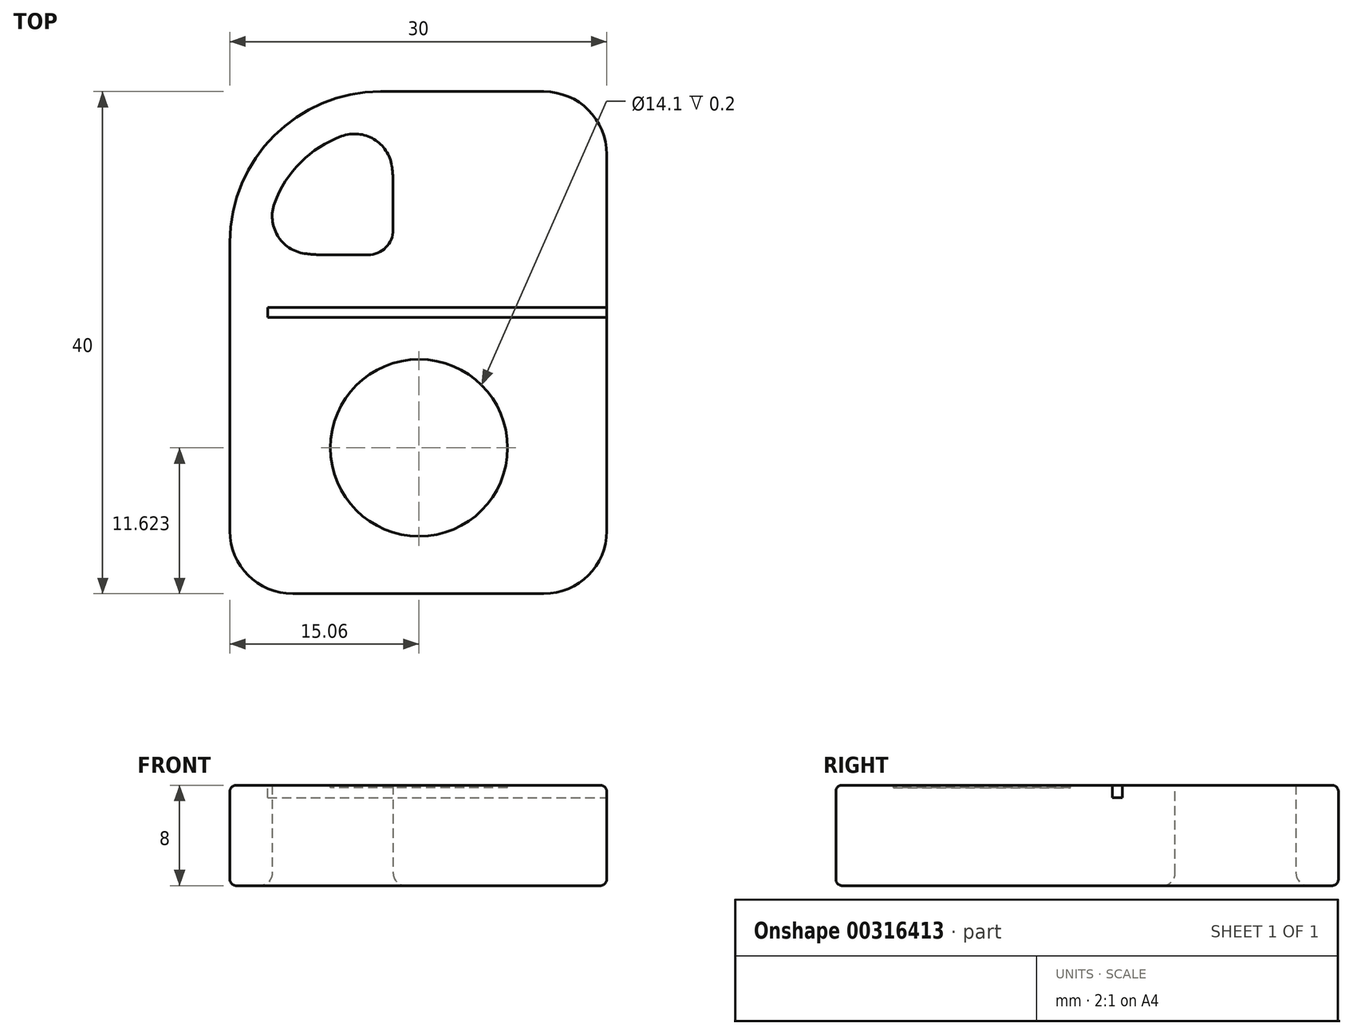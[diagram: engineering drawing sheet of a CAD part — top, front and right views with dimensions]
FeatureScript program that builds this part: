
annotation { "Feature Type Name" : "Feature", "Feature Type Description" : "" }
export const myFeature = defineFeature(function(context is Context, id is Id, definition is map)
    precondition{}
    {
        {
            var Q0;
            Q0=qCreatedBy(makeId("Top.planeOp"),FACE);
            var sketch = newSketch(context, id + "F0", { "sketchPlane" : qUnion([Q0])});
            skLineSegment(sketch, "E0.bottom", {"start": v(0, 0) * mm, "end": v(30, 0) * mm});
            skLineSegment(sketch, "E0.top", {"start": v(0, -40) * mm, "end": v(30, -40) * mm});
            skLineSegment(sketch, "E0.left", {"start": v(0, 0) * mm, "end": v(0, -40) * mm});
            skLineSegment(sketch, "E0.right", {"start": v(30, 0) * mm, "end": v(30, -40) * mm});
            skSolve(sketch);
        }
        {
            var Q0;
            Q0=makeQuery(id+"F0.imprint","IMPRINT",FACE,{"disambiguationData":[TD([[makeQuery(id+"F0.imprint","IMPRINT",EDGE,{"derivedFrom":sQuery(id+"F0.wireOp",EDGE,"E0.bottom")}),-1.0]])]});
            extrude(context, id + "F1", {"entities" : qUnion([Q0]), "depth" : 8 * mm});
        }
        {
            var Q0;
            Q0=makeQuery(id+"F1.opExtrude","SWEPT_EDGE",EDGE,{"disambiguationData":[OSD([sQuery(id+"F0.wireOp",EDGE,"E0.bottom"),sQuery(id+"F0.wireOp",EDGE,"E0.left")])]});
            fillet(context, id + "F2", {"entities" : qUnion([Q0]), "radius" : 12 * mm, "tangentPropagation" : true, "allowEdgeOverflow" : false});
        }
        {
            var Q0;
            Q0=makeQuery(id+"F1.opExtrude","SWEPT_EDGE",EDGE,{"disambiguationData":[OSD([sQuery(id+"F0.wireOp",EDGE,"E0.bottom"),sQuery(id+"F0.wireOp",EDGE,"E0.right")])]});
            var Q1;
            Q1=makeQuery(id+"F1.opExtrude","SWEPT_EDGE",EDGE,{"disambiguationData":[OSD([sQuery(id+"F0.wireOp",EDGE,"E0.top"),sQuery(id+"F0.wireOp",EDGE,"E0.right")])]});
            var Q2;
            Q2=makeQuery(id+"F1.opExtrude","SWEPT_EDGE",EDGE,{"disambiguationData":[OSD([sQuery(id+"F0.wireOp",EDGE,"E0.top"),sQuery(id+"F0.wireOp",EDGE,"E0.left")])]});
            fillet(context, id + "F3", {"entities" : qUnion([Q0, Q1, Q2]), "radius" : 5 * mm, "tangentPropagation" : true, "allowEdgeOverflow" : false});
        }
        {
            var Q0;
            Q0=makeQuery(id+"F1.opExtrude","CAP_FACE",FACE,{"disambiguationData":[OSD([sQuery(id+"F0.wireOp",EDGE,"E0.bottom"),sQuery(id+"F0.wireOp",EDGE,"E0.top"),sQuery(id+"F0.wireOp",EDGE,"E0.left"),sQuery(id+"F0.wireOp",EDGE,"E0.right")])],"isStart":false});
            var sketch = newSketch(context, id + "F4", { "sketchPlane" : qUnion([Q0])});
            skArc(sketch, "E1.0", {"start": v(12, 0) * mm, "mid": v(3.51, -3.51) * mm, "end": v(0, -12) * mm});
            skLineSegment(sketch, "E1.1", {"start": v(12, 0) * mm, "end": v(25, 0) * mm});
            skLineSegment(sketch, "E1.2", {"start": v(0, -12) * mm, "end": v(0, -35) * mm});
            skLineSegment(sketch, "E2.0", {"start": v(3, -12) * mm, "end": v(3, -35) * mm});
            skArc(sketch, "E2.1", {"start": v(12, -3) * mm, "mid": v(5.64, -5.64) * mm, "end": v(3, -12) * mm});
            skLineSegment(sketch, "E2.2", {"start": v(12, -3) * mm, "end": v(25, -3) * mm});
            skLineSegment(sketch, "E3", {"start": v(13, -3) * mm, "end": v(13, -13) * mm});
            skLineSegment(sketch, "E4", {"start": v(13, -13) * mm, "end": v(3, -13) * mm});
            skLineSegment(sketch, "E5.bottom", {"start": v(0, -17.2) * mm, "end": v(30, -17.2) * mm});
            skLineSegment(sketch, "E5.top", {"start": v(0, -18) * mm, "end": v(30, -18) * mm});
            skLineSegment(sketch, "E5.left", {"start": v(0, -17.2) * mm, "end": v(0, -18) * mm});
            skLineSegment(sketch, "E5.right", {"start": v(30, -17.2) * mm, "end": v(30, -18) * mm});
            skSolve(sketch);
        }
        {
            var Q0;
            {var subQ2=sQuery(id+"F4.wireOp",EDGE,"E2.1");Q0=makeQuery(id+"F4.imprint","IMPRINT",FACE,{"disambiguationData":[TD([[makeQuery(id+"F4.imprint","IMPRINT",EDGE,{"derivedFrom":subQ2}),1.0]])]});}
            extrude(context, id + "F5", {"entities" : qUnion([Q0]), "operationType" : NewBodyOperationType.REMOVE, "oppositeDirection" : true, "depth" : 25 * mm});
        }
        {
            var Q0;
            {var subQ5=sQuery(id+"F4.wireOp",EDGE,"E5.right");Q0=makeQuery(id+"F4.imprint","IMPRINT",FACE,{"disambiguationData":[TD([[makeQuery(id+"F4.imprint","IMPRINT",EDGE,{"derivedFrom":subQ5}),-1.0]])]});}
            var Q1;
            {var subQ5=sQuery(id+"F4.wireOp",EDGE,"E5.left");Q1=makeQuery(id+"F4.imprint","IMPRINT",FACE,{"disambiguationData":[TD([[makeQuery(id+"F4.imprint","IMPRINT",EDGE,{"derivedFrom":subQ5}),1.0]])]});}
            extrude(context, id + "F6", {"entities" : qUnion([Q0, Q1]), "operationType" : NewBodyOperationType.REMOVE, "oppositeDirection" : true, "depth" : 1 * mm});
        }
        {
            var Q0;
            Q0=makeQuery(id+"F5.boolean.opBoolean","COPY",EDGE,{"derivedFrom":makeQuery(id+"F5.opExtrude","SWEPT_EDGE",EDGE,{"disambiguationData":[OSD([sQuery(id+"F4.wireOp",EDGE,"E2.2"),sQuery(id+"F4.wireOp",EDGE,"E3")])]})});
            var Q1;
            Q1=makeQuery(id+"F5.boolean.opBoolean","COPY",EDGE,{"derivedFrom":makeQuery(id+"F5.opExtrude","SWEPT_EDGE",EDGE,{"disambiguationData":[OSD([sQuery(id+"F4.wireOp",EDGE,"E2.0"),sQuery(id+"F4.wireOp",EDGE,"E4")])]})});
            fillet(context, id + "F7", {"entities" : qUnion([Q0, Q1]), "radius" : 10 * mm, "tangentPropagation" : true, "allowEdgeOverflow" : false});
        }
        {
            var Q0;
            Q0=makeQuery(id+"F7.opFillet","BLEND_EDGE",EDGE,{"blendedFrom":[makeQuery(id+"F5.boolean.opBoolean","COPY",EDGE,{"derivedFrom":makeQuery(id+"F5.opExtrude","SWEPT_EDGE",EDGE,{"disambiguationData":[OSD([sQuery(id+"F4.wireOp",EDGE,"E2.2"),sQuery(id+"F4.wireOp",EDGE,"E3")])]})}),makeQuery(id+"F5.boolean.opBoolean","COPY",FACE,{"derivedFrom":makeQuery(id+"F5.opExtrude","SWEPT_FACE",FACE,{"disambiguationData":[OSD([sQuery(id+"F4.wireOp",EDGE,"E2.1")])]})})],"blendedInto":[makeQuery(id+"F5.boolean.opBoolean","COPY",FACE,{"derivedFrom":makeQuery(id+"F5.opExtrude","SWEPT_FACE",FACE,{"disambiguationData":[OSD([sQuery(id+"F4.wireOp",EDGE,"E2.1")])]})})]});
            var Q1;
            Q1=makeQuery(id+"F7.opFillet","BLEND_EDGE",EDGE,{"blendedFrom":[makeQuery(id+"F5.boolean.opBoolean","COPY",EDGE,{"derivedFrom":makeQuery(id+"F5.opExtrude","SWEPT_EDGE",EDGE,{"disambiguationData":[OSD([sQuery(id+"F4.wireOp",EDGE,"E2.0"),sQuery(id+"F4.wireOp",EDGE,"E4")])]})}),makeQuery(id+"F5.boolean.opBoolean","COPY",FACE,{"derivedFrom":makeQuery(id+"F5.opExtrude","SWEPT_FACE",FACE,{"disambiguationData":[OSD([sQuery(id+"F4.wireOp",EDGE,"E2.1")])]})})],"blendedInto":[makeQuery(id+"F5.boolean.opBoolean","COPY",FACE,{"derivedFrom":makeQuery(id+"F5.opExtrude","SWEPT_FACE",FACE,{"disambiguationData":[OSD([sQuery(id+"F4.wireOp",EDGE,"E2.1")])]})})]});
            fillet(context, id + "F8", {"entities" : qUnion([Q0, Q1]), "radius" : 3 * mm, "tangentPropagation" : true, "allowEdgeOverflow" : false});
        }
        {
            var Q0;
            Q0=makeQuery(id+"F5.boolean.opBoolean","COPY",EDGE,{"derivedFrom":makeQuery(id+"F5.opExtrude","SWEPT_EDGE",EDGE,{"disambiguationData":[OSD([sQuery(id+"F4.wireOp",EDGE,"E3"),sQuery(id+"F4.wireOp",EDGE,"E4")])]})});
            fillet(context, id + "F9", {"entities" : qUnion([Q0]), "radius" : 2 * mm, "tangentPropagation" : true, "allowEdgeOverflow" : false});
        }
        {
            var Q0;
            {var subQ0=sQuery(id+"F0.wireOp",EDGE,"E0.right");Q0=makeQuery(id+"F6.boolean.opBoolean","SPLIT",EDGE,{"disambiguationData":[TD([makeQuery(id+"F6.opExtrude","SWEPT_FACE",FACE,{"disambiguationData":[OSD([sQuery(id+"F4.wireOp",EDGE,"E5.bottom")])]})])],"derivedFrom":makeQuery(id+"F1.opExtrude","CAP_EDGE",EDGE,{"disambiguationData":[OSD([subQ0])],"isStart":false})});}
            var Q1;
            {var subQ0=sQuery(id+"F0.wireOp",EDGE,"E0.right");Q1=makeQuery(id+"F6.boolean.opBoolean","SPLIT",EDGE,{"disambiguationData":[TD([makeQuery(id+"F6.opExtrude","SWEPT_FACE",FACE,{"disambiguationData":[OSD([sQuery(id+"F4.wireOp",EDGE,"E5.top")])]})])],"derivedFrom":makeQuery(id+"F1.opExtrude","CAP_EDGE",EDGE,{"disambiguationData":[OSD([subQ0])],"isStart":false})});}
            var Q2;
            Q2=makeQuery(id+"F1.opExtrude","CAP_EDGE",EDGE,{"disambiguationData":[OSD([sQuery(id+"F0.wireOp",EDGE,"E0.right")])],"isStart":true});
            fillet(context, id + "F10", {"entities" : qUnion([Q0, Q1, Q2]), "radius" : 0.5 * mm, "tangentPropagation" : true, "allowEdgeOverflow" : false});
        }
        {
            var Q0;
            Q0=makeQuery(id+"F5.boolean.opBoolean","COPY",EDGE,{"derivedFrom":makeQuery(id+"F5.opExtrude","CAP_EDGE",EDGE,{"disambiguationData":[OSD([sQuery(id+"F4.wireOp",EDGE,"E2.1")])],"isStart":true})});
            var Q1;
            Q1=makeQuery(id+"F8.opFillet","BLEND_EDGE",EDGE,{"blendedFrom":[makeQuery(id+"F7.opFillet","BLEND_EDGE",EDGE,{"blendedFrom":[makeQuery(id+"F5.boolean.opBoolean","COPY",EDGE,{"derivedFrom":makeQuery(id+"F5.opExtrude","SWEPT_EDGE",EDGE,{"disambiguationData":[OSD([sQuery(id+"F4.wireOp",EDGE,"E2.2"),sQuery(id+"F4.wireOp",EDGE,"E3")])]})}),makeQuery(id+"F5.boolean.opBoolean","COPY",FACE,{"derivedFrom":makeQuery(id+"F5.opExtrude","SWEPT_FACE",FACE,{"disambiguationData":[OSD([sQuery(id+"F4.wireOp",EDGE,"E2.1")])]})})],"blendedInto":[makeQuery(id+"F5.boolean.opBoolean","COPY",FACE,{"derivedFrom":makeQuery(id+"F5.opExtrude","SWEPT_FACE",FACE,{"disambiguationData":[OSD([sQuery(id+"F4.wireOp",EDGE,"E2.1")])]})})]}),makeQuery(id+"F1.opExtrude","CAP_FACE",FACE,{"disambiguationData":[OSD([sQuery(id+"F0.wireOp",EDGE,"E0.bottom"),sQuery(id+"F0.wireOp",EDGE,"E0.top"),sQuery(id+"F0.wireOp",EDGE,"E0.left"),sQuery(id+"F0.wireOp",EDGE,"E0.right")])],"isStart":true})],"blendedInto":[makeQuery(id+"F1.opExtrude","CAP_FACE",FACE,{"disambiguationData":[OSD([sQuery(id+"F0.wireOp",EDGE,"E0.bottom"),sQuery(id+"F0.wireOp",EDGE,"E0.top"),sQuery(id+"F0.wireOp",EDGE,"E0.left"),sQuery(id+"F0.wireOp",EDGE,"E0.right")])],"isStart":true})]});
            fillet(context, id + "F11", {"entities" : qUnion([Q0, Q1]), "radius" : 1 * mm, "tangentPropagation" : true, "allowEdgeOverflow" : false});
        }
        {
            var Q0;
            {var subQ0=sQuery(id+"F0.wireOp",EDGE,"E0.right");var subQ1=sQuery(id+"F0.wireOp",EDGE,"E0.left");var subQ2=sQuery(id+"F0.wireOp",EDGE,"E0.top");Q0=makeQuery(id+"F6.boolean.opBoolean","SPLIT",FACE,{"disambiguationData":[TD([makeQuery(id+"F1.opExtrude","SWEPT_FACE",FACE,{"disambiguationData":[OSD([subQ2])]})])],"derivedFrom":makeQuery(id+"F1.opExtrude","CAP_FACE",FACE,{"disambiguationData":[OSD([sQuery(id+"F0.wireOp",EDGE,"E0.bottom"),subQ2,subQ1,subQ0])],"isStart":false})});}
            var sketch = newSketch(context, id + "F12", { "sketchPlane" : qUnion([Q0])});
            skCircle(sketch, "E6", {"center": v(15.06, -28.38) * mm, "radius": 7.05 * mm});
            skSolve(sketch);
        }
        {
            var Q0;
            Q0=makeQuery(id+"F12.imprint","IMPRINT",FACE,{"disambiguationData":[TD([[makeQuery(id+"F12.imprint","IMPRINT",EDGE,{"derivedFrom":sQuery(id+"F12.wireOp",EDGE,"E6")}),1.0]])]});
            extrude(context, id + "F13", {"entities" : qUnion([Q0]), "operationType" : NewBodyOperationType.REMOVE, "oppositeDirection" : true, "depth" : 0.2 * mm});
        }
    });
